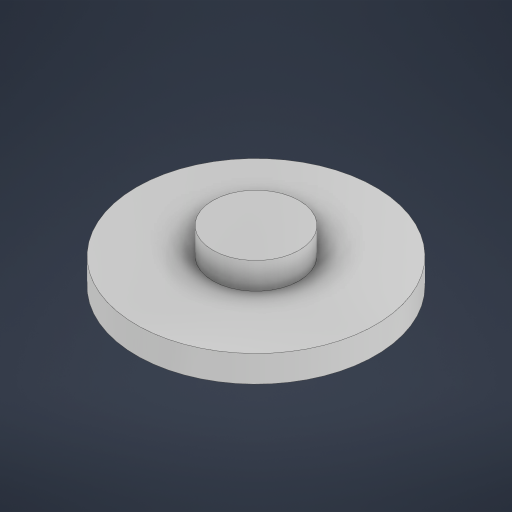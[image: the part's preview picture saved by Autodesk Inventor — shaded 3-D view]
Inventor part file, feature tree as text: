
AUTODESK INVENTOR PART (.ipt)
format: ipt  version: 2024 (Build 280153000, 153)  size: 186,368 bytes
history: native  units: mm
features: extrude x2, sketch x2
ambient origin geometry x8: Origin, YZ Plane, XZ Plane, XY Plane, X Axis, Y Axis, Z Axis, Center Point
bodies: Solid1 (feature_tree)
feature tree (4):
  extrude  "Extrusion1"  Depth=20.0mm TaperAngle=0.0deg
  extrude  "Extrusion2"  Depth=20.0mm TaperAngle=0.0deg
  sketch  "Sketch1"  dims[d0=180.0mm d1=20.0mm d2=0.0mm]
  sketch  "Sketch2"  dims[d3=65.0mm d4=20.0mm d5=0.0mm]
